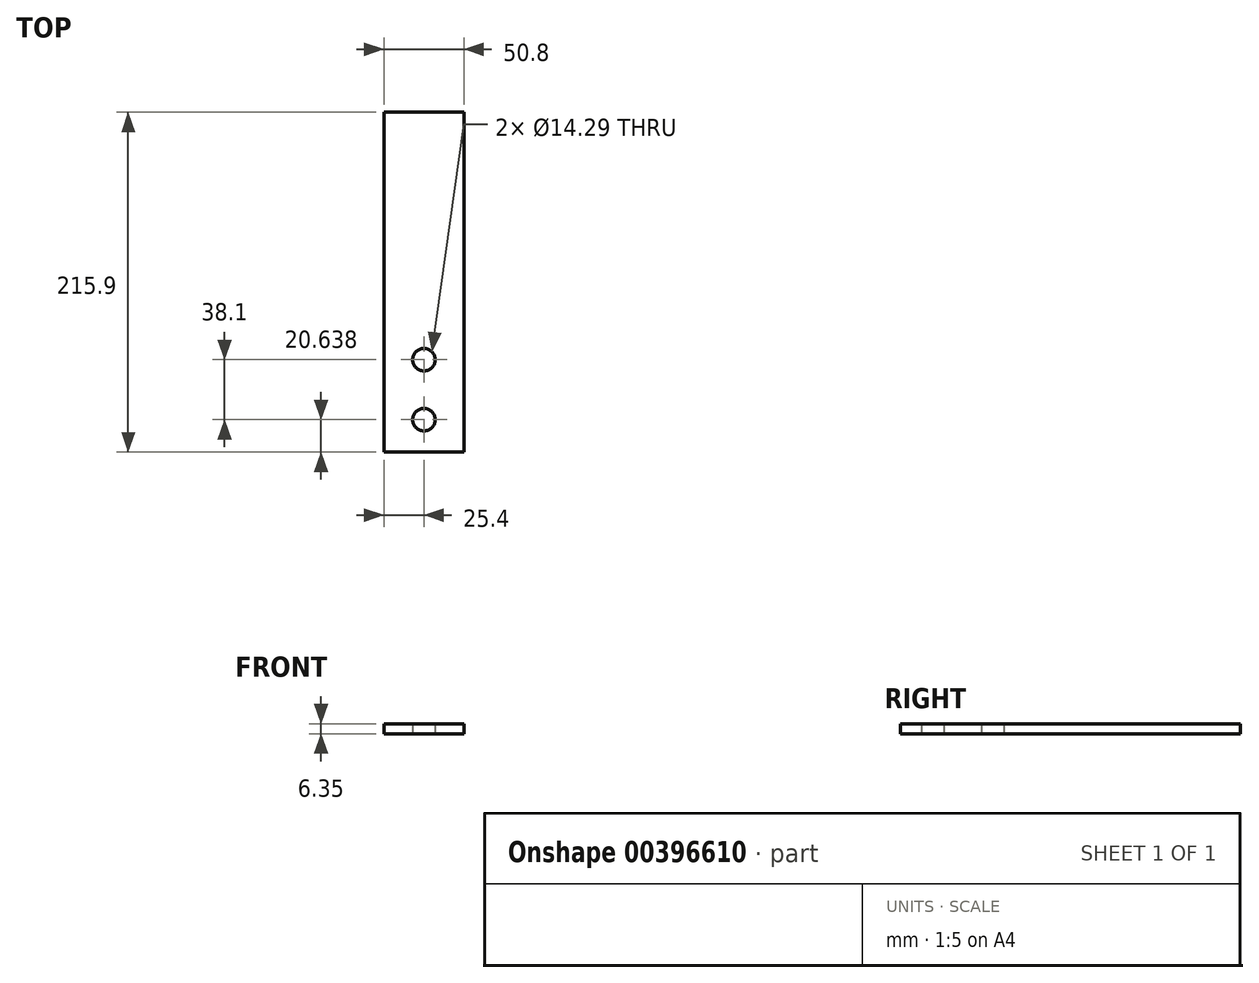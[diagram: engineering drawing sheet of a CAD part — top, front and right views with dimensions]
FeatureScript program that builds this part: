
annotation { "Feature Type Name" : "Feature", "Feature Type Description" : "" }
export const myFeature = defineFeature(function(context is Context, id is Id, definition is map)
    precondition{}
    {
        {
            var Q0;
            Q0=qCreatedBy(makeId("Top.planeOp"),FACE);
            var sketch = newSketch(context, id + "F0", { "sketchPlane" : qUnion([Q0])});
            skLineSegment(sketch, "E0.bottom", {"start": v(25.4, -107.95) * mm, "end": v(-25.4, -107.95) * mm});
            skLineSegment(sketch, "E0.top", {"start": v(25.4, 107.95) * mm, "end": v(-25.4, 107.95) * mm});
            skLineSegment(sketch, "E0.left", {"start": v(25.4, -107.95) * mm, "end": v(25.4, 107.95) * mm});
            skLineSegment(sketch, "E0.right", {"start": v(-25.4, -107.95) * mm, "end": v(-25.4, 107.95) * mm});
            skPoint(sketch, "E0.middle", {"position": v(0, 0) * mm});
            skCircle(sketch, "E1", {"center": v(0, -87.31) * mm, "radius": 7.14 * mm});
            skCircle(sketch, "E2", {"center": v(0, -49.21) * mm, "radius": 7.14 * mm});
            skSolve(sketch);
        }
        {
            var Q0;
            Q0 = qSketchRegion(id + "F0", true);
            extrude(context, id + "F1", {"entities" : qUnion([Q0]), "depth" : 6.35 * mm});
        }
    });
